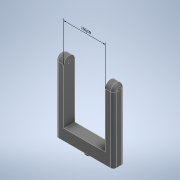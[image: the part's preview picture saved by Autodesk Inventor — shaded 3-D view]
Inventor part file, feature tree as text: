
AUTODESK INVENTOR PART (.ipt)
format: ipt  version: 2021 (Build 250183000, 183)  size: 170,496 bytes
history: native  units: mm
features: extrude x6, sketch x6, other x2, fillet x1
ambient origin geometry x8: Origin, YZ Plane, XZ Plane, XY Plane, X Axis, Y Axis, Z Axis, Center Point
bodies: Solid1 (feature_tree)
feature tree (15):
  other  "Annotations"
  extrude  "Extrusion1"  Depth=40.0mm
  extrude  "Extrusion2"  Depth=40.0mm
  extrude  "Extrusion3"  Depth=30.0mm
  extrude  "Extrusion4"  Depth=30.0mm TaperAngle=0.0deg
  extrude  "Extrusion5"  Depth=10.0mm TaperAngle=0.0deg
  fillet  "Fillet1"  Radius=10.0mm
  extrude  "Extrusion6"  TaperAngle=0.0deg  [1 undecoded]
  sketch  "Sketch1"  dims[d0=20.0mm d1=40.0mm]
  sketch  "Sketch2"  dims[d2=40.0mm d3=40.0mm]
  sketch  "Sketch3"  dims[d4=210.0mm d5=0.0mm d6=30.0mm]
  sketch  "Sketch4"  dims[d7=30.0mm d8=200.0mm d9=0.0mm]
  sketch  "Sketch5"  dims[d10=200.0mm d11=0.0mm d12=200.0mm d13=0.0mm d14=10.0mm]
  sketch  "Sketch6"  dims[d15=10.0mm d16=0.0mm d17=0.0mm d20=10.0mm d21=30.0mm d22=10.0mm d23=0.0mm d18=8.345735mm d19=150.0mm]
  other  "Linear Dimension 1"
note: 1 required parameter value undecoded (feature->parameter linkage not recoverable at this tier; creation-order binding heuristic only, values carry confidence <= 0.55)
